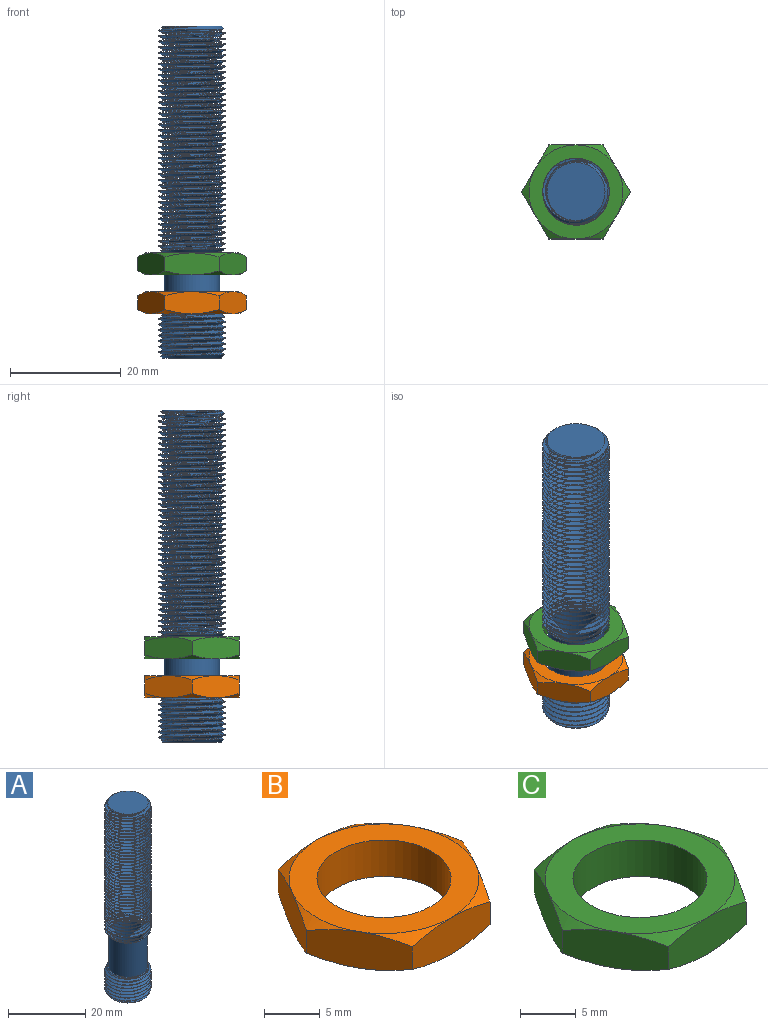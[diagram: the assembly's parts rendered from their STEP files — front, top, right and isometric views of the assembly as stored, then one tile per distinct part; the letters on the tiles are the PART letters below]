
ASSEMBLY  parts=3 mates=2
PART A: 38 faces, bbox 13.9x12x60.8 mm
  f0: plane 8.2x8.09mm, normal (0,0,-1), area 47.8mm2, adj f1,f4,f7,f27,f28,f29,f30,f31
  f1: cylinder r=0.51mm len=8.3mm, axis (0,0,1), area 26.5mm2, adj f0,f2
  f2: torus R=0.01mm, axis (0,0,1), area 1.6mm2, adj f1,f3
  f3: plane 0.02x0.02mm, normal (0,0,-1), area 0mm2, adj f2
  f4: cylinder r=0.51mm len=8.3mm, axis (0,0,1), area 26.5mm2, adj f0,f5
  f5: torus R=0.01mm, axis (0,0,1), area 1.6mm2, adj f4,f6
  f6: plane 0.02x0.02mm, normal (0,0,-1), area 0mm2, adj f5
  f7: cylinder r=4.1mm len=8.8mm, axis (0,0,-1), area 209.9mm2, adj f0,f8,f27,f31
  f8: plane 10.5x10.5mm, normal (0,0,-1), area 35.5mm2, adj f7,f9,f27,f28,f29,f30,f31
  f9: cone r=5.25mm half-angle=45deg, axis (0,0,1), area 16.7mm2, adj f8,f10,f25,f26
  f10: cylinder r=5.35mm len=10.7mm, axis (0,0,-1), area 32.9mm2, adj f9,f11,f24,f25
  f11: cone r=6mm half-angle=45deg, axis (0,0,-1), area 20.9mm2, adj f10,f12,f13,f24,f25
  f12: cylinder r=6mm len=12mm, axis (0,0,-1), area 30.4mm2, adj f11,f24,f25,f26
  f13: plane 10.5x10.5mm, normal (0,0,1), area 8.1mm2, adj f11,f14
  f14: cylinder r=5mm len=11mm, axis (0,0,-1), area 345.6mm2, adj f13,f15
  f15: plane 10.5x10.5mm, normal (0,0,-1), area 8.1mm2, adj f14,f16
  f16: cone r=6mm half-angle=45deg, axis (0,0,1), area 19.9mm2, adj f15,f17,f21,f22,f23
  f17: cylinder r=5.35mm len=40.8mm, axis (0,0,-1), area 92mm2, adj f16,f18,f21,f23
  f18: cone r=5.25mm half-angle=45deg, axis (0,0,-1), area 20.9mm2, adj f17,f19,f20,f21,f23
  f19: cylinder r=6mm len=39.5mm, axis (0,0,1), area -446.8mm2, adj f18,f21,f22,f23
  f20: plane 10.5x10.5mm, normal (0,0,1), area 86.6mm2, adj f18
  f21: bspline ~41.38x13.86mm, area 1118.6mm2, adj f16,f17,f18,f19,f22
  f22: cone r=6mm half-angle=45deg, axis (0,0,1), area 0.3mm2, adj f16,f19,f21,f23
  f23: bspline ~41.38x13.86mm, area 1091.5mm2, adj f16,f17,f18,f19,f22
  f24: bspline ~12x12mm, area 191.2mm2, adj f10,f11,f12,f26
  f25: bspline ~12x12mm, area 190.3mm2, adj f9,f10,f11,f12,f26
  f26: cone r=5.25mm half-angle=45deg, axis (0,0,1), area 4.2mm2, adj f9,f12,f24,f25
  f27: cylinder r=0.2mm len=8.8mm, axis (0,0,-1), area 3.2mm2, adj f0,f7,f8,f28
  f28: plane 8.8x0.39mm, normal (1,0,0), area 3.5mm2, adj f0,f8,f27,f29
  f29: cylinder r=0.7mm len=8.8mm, axis (0,0,-1), area 19.4mm2, adj f0,f8,f28,f30
  f30: plane 8.8x0.39mm, normal (-1,0,0), area 3.5mm2, adj f0,f8,f29,f31
  f31: cylinder r=0.2mm len=8.8mm, axis (0,0,-1), area 3.2mm2, adj f0,f7,f8,f30
  f32: cylinder r=0.51mm len=8.3mm, axis (0,0,1), area 26.5mm2, adj f0,f33
  f33: torus R=0.01mm, axis (0,0,1), area 1.6mm2, adj f32,f34
  f34: plane 0.02x0.02mm, normal (0,0,-1), area 0mm2, adj f33
  f35: cylinder r=0.51mm len=8.3mm, axis (0,0,1), area 26.5mm2, adj f0,f36
  f36: torus R=0.01mm, axis (0,0,1), area 1.6mm2, adj f35,f37
  f37: plane 0.02x0.02mm, normal (0,0,-1), area 0mm2, adj f36
PART B: 21 faces, bbox 20.4x20.4x4.8 mm
  f0: plane 17x17mm, normal (0,0,1), area 113.9mm2, adj f8,f9,f10,f11,f12,f13,f14
  f1: plane 9.31x5.71mm, normal (-0.87,0.5,0), area 34.1mm2, adj f2,f6,f9,f14,f15,f16
  f2: plane 9.31x5.71mm, normal (-0.87,-0.5,0), area 34.1mm2, adj f1,f3,f13,f14,f15,f20
  f3: plane 10.63x4.81mm, normal (0,-1,0), area 34.1mm2, adj f2,f4,f12,f13,f19,f20
  f4: plane 9.31x5.71mm, normal (0.87,-0.5,0), area 34.1mm2, adj f3,f5,f11,f12,f18,f19
  f5: plane 9.31x5.71mm, normal (0.87,0.5,0), area 34.1mm2, adj f4,f6,f10,f11,f17,f18
  f6: plane 10.63x4.81mm, normal (0,1,0), area 34.1mm2, adj f1,f5,f9,f10,f16,f17
  f7: plane 17x17mm, normal (0,0,-1), area 113.9mm2, adj f8,f15,f16,f17,f18,f19,f20
  f8: cylinder r=6mm len=12mm, axis (0,0,-1), area 150.8mm2, adj f0,f7
  f9: cone r=8.5mm half-angle=60deg, axis (0,0,-1), area 7.1mm2, adj f0,f1,f6
  f10: cone r=8.5mm half-angle=60deg, axis (0,0,-1), area 7.1mm2, adj f0,f5,f6
  f11: cone r=8.5mm half-angle=60deg, axis (0,0,-1), area 7.1mm2, adj f0,f4,f5
  f12: cone r=8.5mm half-angle=60deg, axis (0,0,-1), area 7.1mm2, adj f0,f3,f4
  f13: cone r=8.5mm half-angle=60deg, axis (0,0,-1), area 7.1mm2, adj f0,f2,f3
  f14: cone r=8.5mm half-angle=60deg, axis (0,0,-1), area 7.1mm2, adj f0,f1,f2
  f15: cone r=8.5mm half-angle=60deg, axis (0,0,1), area 7.1mm2, adj f1,f2,f7
  f16: cone r=8.5mm half-angle=60deg, axis (0,0,1), area 7.1mm2, adj f1,f6,f7
  f17: cone r=8.5mm half-angle=60deg, axis (0,0,1), area 7.1mm2, adj f5,f6,f7
  f18: cone r=8.5mm half-angle=60deg, axis (0,0,1), area 7.1mm2, adj f4,f5,f7
  f19: cone r=8.5mm half-angle=60deg, axis (0,0,1), area 7.1mm2, adj f3,f4,f7
  f20: cone r=8.5mm half-angle=60deg, axis (0,0,1), area 7.1mm2, adj f2,f3,f7
PART C: 21 faces, bbox 20.4x20.4x4.8 mm
  f0: plane 17x17mm, normal (0,0,-1), area 113.9mm2, adj f8,f9,f10,f11,f12,f13,f14
  f1: plane 9.31x5.71mm, normal (-0.87,0.5,0), area 34.1mm2, adj f2,f6,f9,f14,f15,f16
  f2: plane 9.31x5.71mm, normal (-0.87,-0.5,0), area 34.1mm2, adj f1,f3,f13,f14,f15,f20
  f3: plane 10.63x4.81mm, normal (0,-1,0), area 34.1mm2, adj f2,f4,f12,f13,f19,f20
  f4: plane 9.31x5.71mm, normal (0.87,-0.5,0), area 34.1mm2, adj f3,f5,f11,f12,f18,f19
  f5: plane 9.31x5.71mm, normal (0.87,0.5,0), area 34.1mm2, adj f4,f6,f10,f11,f17,f18
  f6: plane 10.63x4.81mm, normal (0,1,0), area 34.1mm2, adj f1,f5,f9,f10,f16,f17
  f7: plane 17x17mm, normal (0,0,1), area 113.9mm2, adj f8,f15,f16,f17,f18,f19,f20
  f8: cylinder r=6mm len=12mm, axis (0,0,1), area 150.8mm2, adj f0,f7
  f9: cone r=8.5mm half-angle=60deg, axis (0,0,1), area 7.1mm2, adj f0,f1,f6
  f10: cone r=8.5mm half-angle=60deg, axis (0,0,1), area 7.1mm2, adj f0,f5,f6
  f11: cone r=8.5mm half-angle=60deg, axis (0,0,1), area 7.1mm2, adj f0,f4,f5
  f12: cone r=8.5mm half-angle=60deg, axis (0,0,1), area 7.1mm2, adj f0,f3,f4
  f13: cone r=8.5mm half-angle=60deg, axis (0,0,1), area 7.1mm2, adj f0,f2,f3
  f14: cone r=8.5mm half-angle=60deg, axis (0,0,1), area 7.1mm2, adj f0,f1,f2
  f15: cone r=8.5mm half-angle=60deg, axis (0,0,-1), area 7.1mm2, adj f1,f2,f7
  f16: cone r=8.5mm half-angle=60deg, axis (0,0,-1), area 7.1mm2, adj f1,f6,f7
  f17: cone r=8.5mm half-angle=60deg, axis (0,0,-1), area 7.1mm2, adj f5,f6,f7
  f18: cone r=8.5mm half-angle=60deg, axis (0,0,-1), area 7.1mm2, adj f4,f5,f7
  f19: cone r=8.5mm half-angle=60deg, axis (0,0,-1), area 7.1mm2, adj f3,f4,f7
  f20: cone r=8.5mm half-angle=60deg, axis (0,0,-1), area 7.1mm2, adj f2,f3,f7
PLACE A t=(-12.38,-14.44,18.96)mm
PLACE B t=(-12.38,-14.44,-16.04)mm
PLACE C t=(-12.38,-14.44,-0.04)mm
MATE fastened C.f8 <-> A.f7  axis (0,0,1) through (-12.38,-14.44,-22.04)mm
MATE fastened B.f8 <-> A.f7  axis (0,0,-1) through (-12.38,-14.44,-33.04)mm
